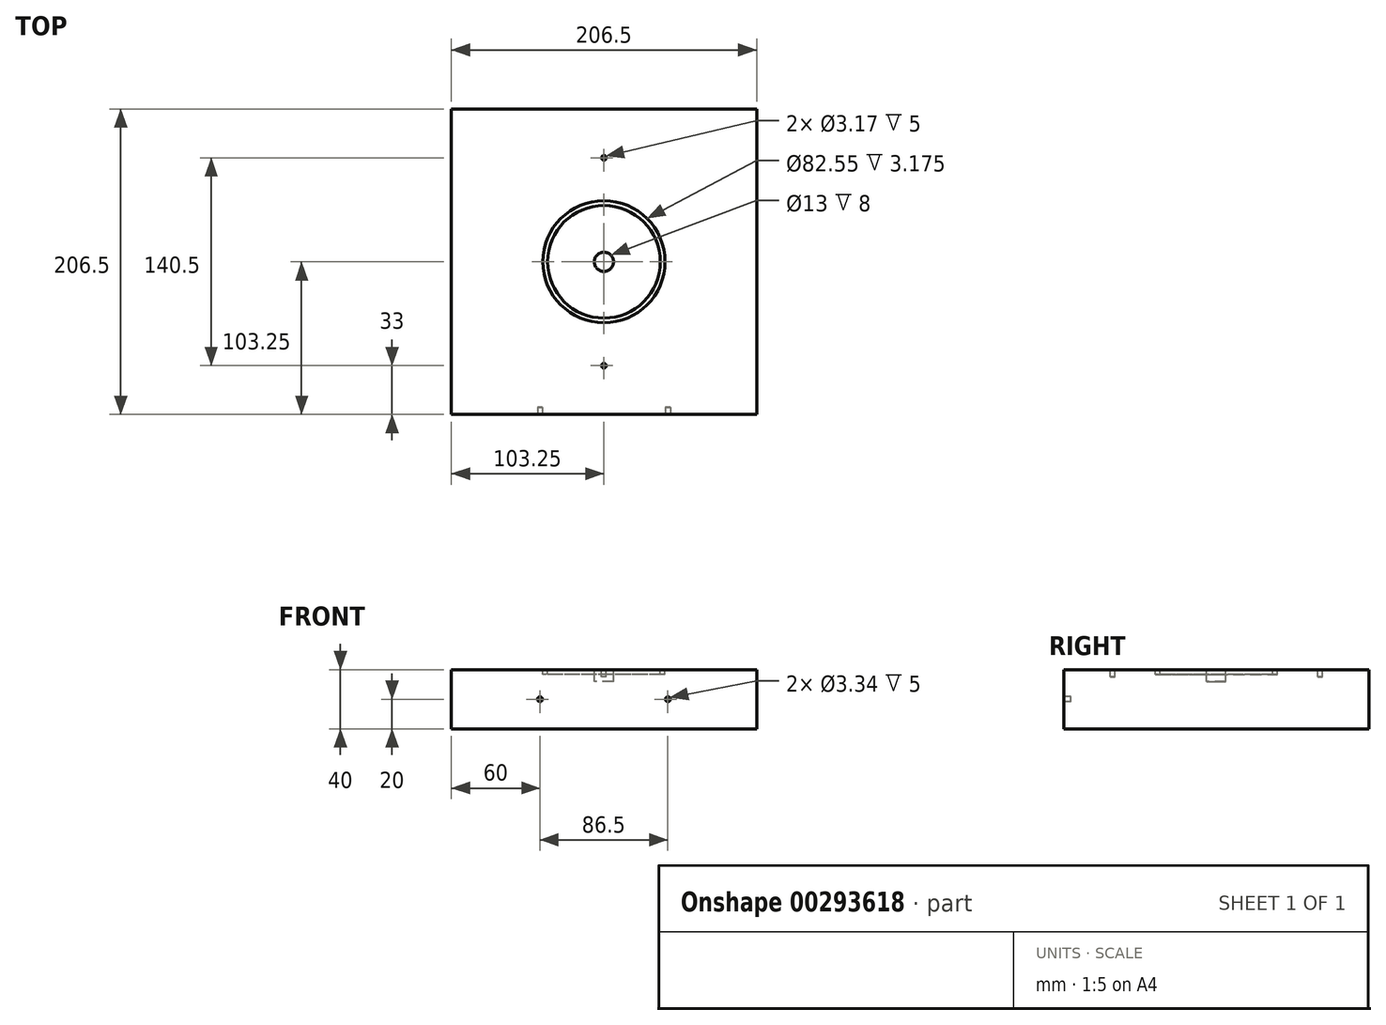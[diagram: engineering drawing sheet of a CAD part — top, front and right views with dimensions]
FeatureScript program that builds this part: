
annotation { "Feature Type Name" : "Feature", "Feature Type Description" : "" }
export const myFeature = defineFeature(function(context is Context, id is Id, definition is map)
    precondition{}
    {
        {
            var Q0;
            Q0=qCreatedBy(makeId("Top.planeOp"),FACE);
            var sketch = newSketch(context, id + "F0", { "sketchPlane" : qUnion([Q0])});
            skLineSegment(sketch, "E0.bottom", {"start": v(103.25, 103.25) * mm, "end": v(-103.25, 103.25) * mm});
            skLineSegment(sketch, "E0.top", {"start": v(103.25, -103.25) * mm, "end": v(-103.25, -103.25) * mm});
            skLineSegment(sketch, "E0.left", {"start": v(103.25, 103.25) * mm, "end": v(103.25, -103.25) * mm});
            skLineSegment(sketch, "E0.right", {"start": v(-103.25, 103.25) * mm, "end": v(-103.25, -103.25) * mm});
            skPoint(sketch, "E0.middle", {"position": v(0, 0) * mm});
            skSolve(sketch);
        }
        {
            var Q0;
            Q0 = qSketchRegion(id + "F0", true);
            extrude(context, id + "F1", {"entities" : qUnion([Q0]), "depth" : 40 * mm});
        }
        {
            var Q0;
            Q0=makeQuery(id+"F1.opExtrude","CAP_FACE",FACE,{"disambiguationData":[OSD([sQuery(id+"F0.wireOp",EDGE,"E0.bottom"),sQuery(id+"F0.wireOp",EDGE,"E0.top"),sQuery(id+"F0.wireOp",EDGE,"E0.left"),sQuery(id+"F0.wireOp",EDGE,"E0.right")])],"isStart":false});
            var sketch = newSketch(context, id + "F2", { "sketchPlane" : qUnion([Q0])});
            skCircle(sketch, "E1", {"center": v(0, 0) * mm, "radius": 41.28 * mm});
            skCircle(sketch, "E2", {"center": v(0, 0) * mm, "radius": 38.1 * mm});
            skSolve(sketch);
        }
        {
            var Q0;
            Q0 = qSketchRegion(id + "F2", true);
            extrude(context, id + "F3", {"entities" : qUnion([Q0]), "operationType" : NewBodyOperationType.REMOVE, "oppositeDirection" : true, "offsetDistance" : 25.4 * mm, "depth" : 3.17 * mm});
        }
        {
            var Q0;
            Q0=makeQuery(id+"F3.boolean.opBoolean","SPLIT",FACE,{"disambiguationData":[TD([makeQuery(id+"F3.opExtrude","SWEPT_FACE",FACE,{"disambiguationData":[OSD([sQuery(id+"F2.wireOp",EDGE,"E2")])]})])],"derivedFrom":makeQuery(id+"F1.opExtrude","CAP_FACE",FACE,{"disambiguationData":[OSD([sQuery(id+"F0.wireOp",EDGE,"E0.bottom"),sQuery(id+"F0.wireOp",EDGE,"E0.top"),sQuery(id+"F0.wireOp",EDGE,"E0.left"),sQuery(id+"F0.wireOp",EDGE,"E0.right")])],"isStart":false})});
            var sketch = newSketch(context, id + "F4", { "sketchPlane" : qUnion([Q0])});
            skCircle(sketch, "E3", {"center": v(0, 0) * mm, "radius": 6.5 * mm});
            skSolve(sketch);
        }
        {
            var Q0;
            Q0 = qSketchRegion(id + "F4", true);
            extrude(context, id + "F5", {"entities" : qUnion([Q0]), "operationType" : NewBodyOperationType.REMOVE, "oppositeDirection" : true, "offsetDistance" : 25.4 * mm, "depth" : 8 * mm});
        }
        {
            var Q0;
            {var subQ0=sQuery(id+"F0.wireOp",EDGE,"E0.left");var subQ1=sQuery(id+"F0.wireOp",EDGE,"E0.top");var subQ2=sQuery(id+"F0.wireOp",EDGE,"E0.right");var subQ3=sQuery(id+"F0.wireOp",EDGE,"E0.bottom");Q0=makeQuery(id+"F3.boolean.opBoolean","SPLIT",FACE,{"disambiguationData":[TD([makeQuery(id+"F1.opExtrude","SWEPT_FACE",FACE,{"disambiguationData":[OSD([subQ3])]})])],"derivedFrom":makeQuery(id+"F1.opExtrude","CAP_FACE",FACE,{"disambiguationData":[OSD([subQ3,subQ1,subQ0,subQ2])],"isStart":false})});}
            var sketch = newSketch(context, id + "F6", { "sketchPlane" : qUnion([Q0])});
            skCircle(sketch, "E4", {"center": v(0, 70.25) * mm, "radius": 1.59 * mm});
            skCircle(sketch, "E5", {"center": v(0, -70.25) * mm, "radius": 1.59 * mm});
            skSolve(sketch);
        }
        {
            var Q0;
            Q0=makeQuery(id+"F1.opExtrude","SWEPT_FACE",FACE,{"disambiguationData":[OSD([sQuery(id+"F0.wireOp",EDGE,"E0.top")])]});
            var sketch = newSketch(context, id + "F7", { "sketchPlane" : qUnion([Q0])});
            skCircle(sketch, "E6", {"center": v(-43.25, 20) * mm, "radius": 1.67 * mm});
            skCircle(sketch, "E7", {"center": v(43.25, 20) * mm, "radius": 1.67 * mm});
            skSolve(sketch);
        }
        {
            var Q0;
            Q0 = qSketchRegion(id + "F6", true);
            extrude(context, id + "F8", {"entities" : qUnion([Q0]), "operationType" : NewBodyOperationType.REMOVE, "oppositeDirection" : true, "depth" : 5 * mm});
        }
        {
            var Q0;
            Q0 = qSketchRegion(id + "F7", true);
            extrude(context, id + "F9", {"entities" : qUnion([Q0]), "operationType" : NewBodyOperationType.REMOVE, "oppositeDirection" : true, "depth" : 5 * mm});
        }
    });
